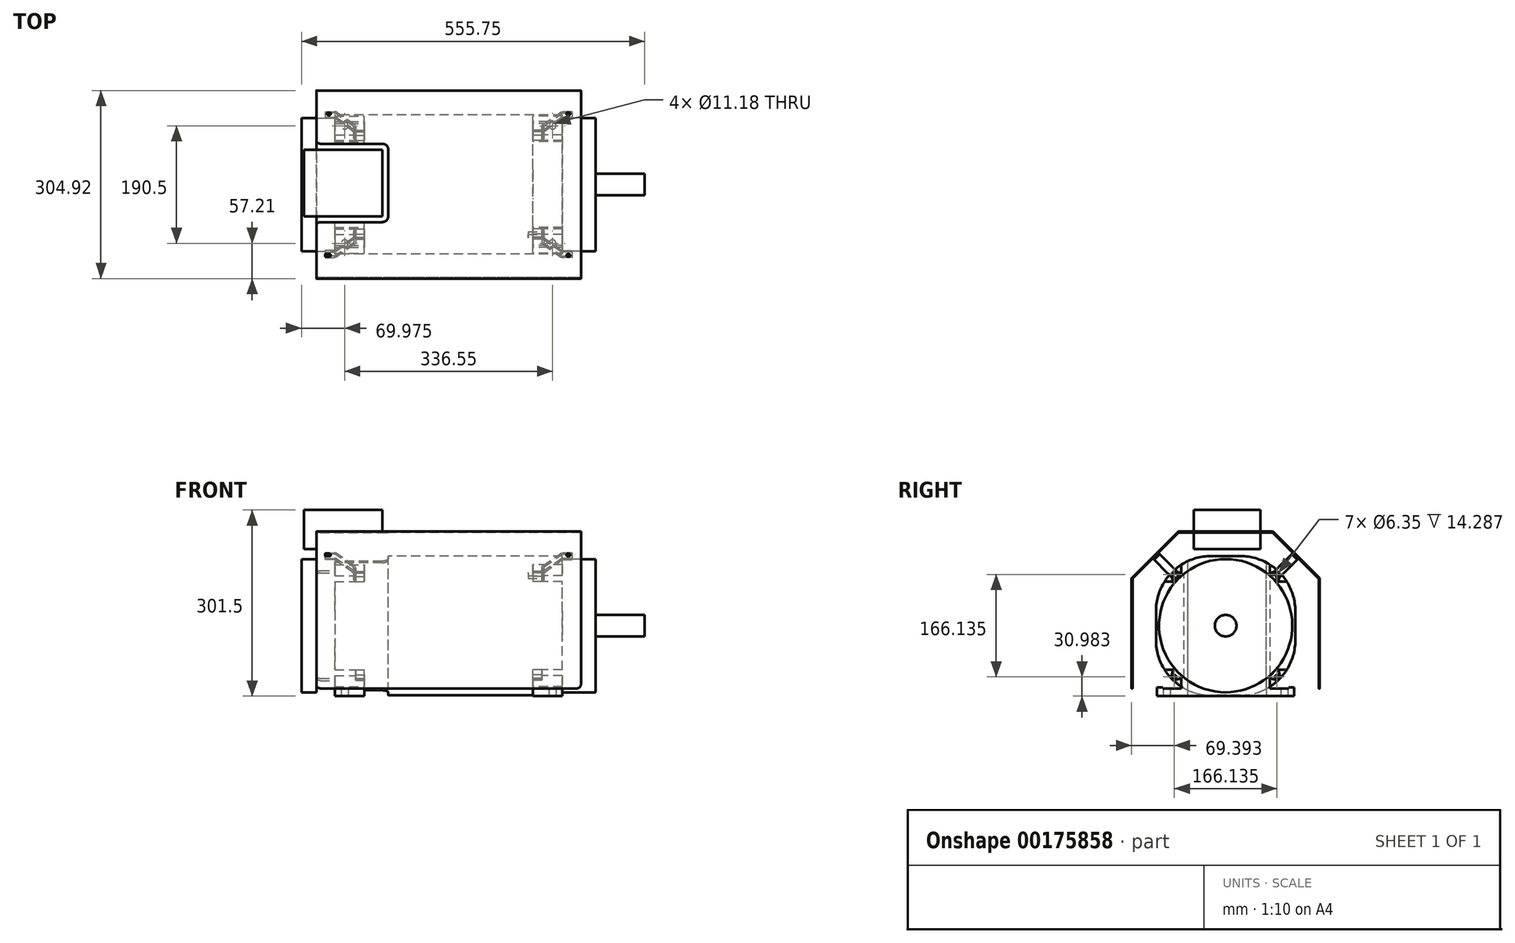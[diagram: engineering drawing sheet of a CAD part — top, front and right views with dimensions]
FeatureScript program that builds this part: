
annotation { "Feature Type Name" : "Feature", "Feature Type Description" : "" }
export const myFeature = defineFeature(function(context is Context, id is Id, definition is map)
    precondition{}
    {
        {
            var Q0;
            Q0=qCreatedBy(makeId("Right.planeOp"),FACE);
            var sketch = newSketch(context, id + "F0", { "sketchPlane" : qUnion([Q0])});
            skLineSegment(sketch, "E0.bottom", {"start": v(23.88, 112.78) * mm, "end": v(-23.88, 112.78) * mm});
            skLineSegment(sketch, "E0.top", {"start": v(23.88, -112.78) * mm, "end": v(-23.88, -112.78) * mm});
            skLineSegment(sketch, "E0.left", {"start": v(112.78, 23.88) * mm, "end": v(112.78, -23.88) * mm});
            skLineSegment(sketch, "E0.right", {"start": v(-112.78, 23.88) * mm, "end": v(-112.78, -23.88) * mm});
            skPoint(sketch, "E0.middle", {"position": v(0, 0) * mm});
            skPoint(sketch, "E1.visualSharp", {"position": v(112.78, 112.78) * mm});
            skArc(sketch, "E1.filletArc", {"start": v(112.78, 23.88) * mm, "mid": v(86.74, 86.74) * mm, "end": v(23.88, 112.78) * mm});
            skPoint(sketch, "E2.visualSharp", {"position": v(112.78, -112.78) * mm});
            skArc(sketch, "E2.filletArc", {"start": v(23.88, -112.78) * mm, "mid": v(86.74, -86.74) * mm, "end": v(112.78, -23.88) * mm});
            skPoint(sketch, "E3.visualSharp", {"position": v(-112.78, -112.78) * mm});
            skArc(sketch, "E3.filletArc", {"start": v(-112.78, -23.88) * mm, "mid": v(-86.74, -86.74) * mm, "end": v(-23.88, -112.78) * mm});
            skPoint(sketch, "E4.visualSharp", {"position": v(-112.78, 112.78) * mm});
            skArc(sketch, "E4.filletArc", {"start": v(-23.88, 112.78) * mm, "mid": v(-86.74, 86.74) * mm, "end": v(-112.78, 23.88) * mm});
            skSolve(sketch);
        }
        {
            var Q0;
            Q0 = qSketchRegion(id + "F0", true);
            extrude(context, id + "F1", {"entities" : qUnion([Q0]), "endBound" : BoundingType.SYMMETRIC, "depth" : 273.05 * mm});
        }
        {
            var Q0;
            Q0=makeQuery(id+"F1.opExtrude","CAP_FACE",FACE,{"disambiguationData":[OSD([sQuery(id+"F0.wireOp",EDGE,"E0.bottom"),sQuery(id+"F0.wireOp",EDGE,"E0.top"),sQuery(id+"F0.wireOp",EDGE,"E0.left"),sQuery(id+"F0.wireOp",EDGE,"E0.right"),sQuery(id+"F0.wireOp",EDGE,"E1.filletArc"),sQuery(id+"F0.wireOp",EDGE,"E2.filletArc"),sQuery(id+"F0.wireOp",EDGE,"E3.filletArc"),sQuery(id+"F0.wireOp",EDGE,"E4.filletArc")])],"isStart":false});
            var sketch = newSketch(context, id + "F2", { "sketchPlane" : qUnion([Q0])});
            skLineSegment(sketch, "E5.0", {"start": v(23.88, 112.78) * mm, "end": v(-23.88, 112.78) * mm});
            skArc(sketch, "E6.0", {"start": v(-23.88, 112.78) * mm, "mid": v(-86.74, 86.74) * mm, "end": v(-112.78, 23.88) * mm});
            skLineSegment(sketch, "E6.1", {"start": v(-112.78, 23.88) * mm, "end": v(-112.78, -23.88) * mm});
            skArc(sketch, "E6.2", {"start": v(-112.78, -23.88) * mm, "mid": v(-86.74, -86.74) * mm, "end": v(-23.88, -112.78) * mm});
            skLineSegment(sketch, "E6.3", {"start": v(23.88, -112.78) * mm, "end": v(-23.88, -112.78) * mm});
            skArc(sketch, "E6.4", {"start": v(23.88, -112.78) * mm, "mid": v(86.74, -86.74) * mm, "end": v(112.78, -23.88) * mm});
            skLineSegment(sketch, "E6.5", {"start": v(112.78, 23.88) * mm, "end": v(112.78, -23.88) * mm});
            skArc(sketch, "E6.6", {"start": v(112.78, 23.88) * mm, "mid": v(86.74, 86.74) * mm, "end": v(23.88, 112.78) * mm});
            skLineSegment(sketch, "E7.bottom", {"start": v(-101.82, 71.66) * mm, "end": v(-71.66, 71.66) * mm});
            skLineSegment(sketch, "E7.top", {"start": v(-101.82, 101.82) * mm, "end": v(-71.66, 101.82) * mm});
            skLineSegment(sketch, "E7.left", {"start": v(-101.82, 71.66) * mm, "end": v(-101.82, 101.82) * mm});
            skLineSegment(sketch, "E7.right", {"start": v(-71.66, 71.66) * mm, "end": v(-71.66, 101.82) * mm});
            skPoint(sketch, "E7.middle", {"position": v(-86.74, 86.74) * mm});
            skCircle(sketch, "E8", {"center": v(0, 0) * mm, "radius": 107.95 * mm});
            skLineSegment(sketch, "E9.1.0", {"start": v(-101.82, -101.82) * mm, "end": v(-101.82, -71.66) * mm});
            skLineSegment(sketch, "E9.1.1", {"start": v(-71.66, -101.82) * mm, "end": v(-101.82, -101.82) * mm});
            skLineSegment(sketch, "E9.1.2", {"start": v(-71.66, -101.82) * mm, "end": v(-71.66, -71.66) * mm});
            skLineSegment(sketch, "E9.1.3", {"start": v(-71.66, -71.66) * mm, "end": v(-101.82, -71.66) * mm});
            skLineSegment(sketch, "E9.2.0", {"start": v(101.82, -101.82) * mm, "end": v(71.66, -101.82) * mm});
            skLineSegment(sketch, "E9.2.1", {"start": v(101.82, -71.66) * mm, "end": v(101.82, -101.82) * mm});
            skLineSegment(sketch, "E9.2.2", {"start": v(101.82, -71.66) * mm, "end": v(71.66, -71.66) * mm});
            skLineSegment(sketch, "E9.2.3", {"start": v(71.66, -71.66) * mm, "end": v(71.66, -101.82) * mm});
            skLineSegment(sketch, "E9.3.0", {"start": v(101.82, 101.82) * mm, "end": v(101.82, 71.66) * mm});
            skLineSegment(sketch, "E9.3.1", {"start": v(71.66, 101.82) * mm, "end": v(101.82, 101.82) * mm});
            skLineSegment(sketch, "E9.3.2", {"start": v(71.66, 101.82) * mm, "end": v(71.66, 71.66) * mm});
            skLineSegment(sketch, "E9.3.3", {"start": v(71.66, 71.66) * mm, "end": v(101.82, 71.66) * mm});
            skLineSegment(sketch, "E10.bottom", {"start": v(-111, -114.05) * mm, "end": v(111, -114.05) * mm});
            skLineSegment(sketch, "E10.top", {"start": v(-111, -100.08) * mm, "end": v(111, -100.08) * mm});
            skLineSegment(sketch, "E10.left", {"start": v(-111, -114.05) * mm, "end": v(-111, -100.08) * mm});
            skLineSegment(sketch, "E10.right", {"start": v(111, -114.05) * mm, "end": v(111, -100.08) * mm});
            skLineSegment(sketch, "E11", {"start": v(0, -114.05) * mm, "end": v(0, -112.78) * mm});
            skPoint(sketch, "E11.endSnap0", {"position": v(0, -100.08) * mm});
            skSolve(sketch);
        }
        {
            var Q0;
            {var subQ9=sQuery(id+"F2.wireOp",EDGE,"E6.1");Q0=makeQuery(id+"F2.imprint","IMPRINT",FACE,{"disambiguationData":[TD([[makeQuery(id+"F2.imprint","IMPRINT",EDGE,{"derivedFrom":subQ9}),1.0]])]});}
            var Q1;
            {var subQ15=sQuery(id+"F2.wireOp",EDGE,"E7.right");var subQ16=sQuery(id+"F2.wireOp",EDGE,"E7.bottom");var subQ17=makeQuery(id+"F2.imprint","INTERSECT",VERTEX,{"derivedFrom":[subQ16,subQ15]});Q1=makeQuery(id+"F2.imprint","IMPRINT",FACE,{"disambiguationData":[TD([[makeQuery(id+"F2.imprint","IMPRINT",EDGE,{"disambiguationData":[TD([[subQ17,1.0]])],"derivedFrom":subQ16}),-1.0]])]});}
            var Q2;
            {var subQ6=sQuery(id+"F2.wireOp",EDGE,"E6.5");Q2=makeQuery(id+"F2.imprint","IMPRINT",FACE,{"disambiguationData":[TD([[makeQuery(id+"F2.imprint","IMPRINT",EDGE,{"derivedFrom":subQ6}),-1.0]])]});}
            var Q3;
            {var subQ8=sQuery(id+"F2.wireOp",EDGE,"E5.0");Q3=makeQuery(id+"F2.imprint","IMPRINT",FACE,{"disambiguationData":[TD([[makeQuery(id+"F2.imprint","IMPRINT",EDGE,{"derivedFrom":subQ8}),1.0]])]});}
            var Q4;
            {var subQ5=sQuery(id+"F2.wireOp",EDGE,"E6.3");Q4=makeQuery(id+"F2.imprint","IMPRINT",FACE,{"disambiguationData":[TD([[makeQuery(id+"F2.imprint","IMPRINT",EDGE,{"derivedFrom":subQ5}),-1.0]])]});}
            var Q5;
            {var subQ0=sQuery(id+"F2.wireOp",EDGE,"E9.1.3");var subQ1=sQuery(id+"F2.wireOp",EDGE,"E8");var subQ2=makeQuery(id+"F2.imprint","INTERSECT",VERTEX,{"derivedFrom":[subQ1,subQ0]});Q5=makeQuery(id+"F2.imprint","IMPRINT",FACE,{"disambiguationData":[TD([[makeQuery(id+"F2.imprint","IMPRINT",EDGE,{"disambiguationData":[TD([[subQ2,-1.0]])],"derivedFrom":subQ1}),1.0]])]});}
            var Q6;
            {var subQ0=sQuery(id+"F2.wireOp",EDGE,"E7.right");var subQ1=sQuery(id+"F2.wireOp",EDGE,"E7.bottom");var subQ2=makeQuery(id+"F2.imprint","INTERSECT",VERTEX,{"derivedFrom":[subQ1,subQ0]});Q6=makeQuery(id+"F2.imprint","IMPRINT",FACE,{"disambiguationData":[TD([[makeQuery(id+"F2.imprint","IMPRINT",EDGE,{"disambiguationData":[TD([[subQ2,1.0]])],"derivedFrom":subQ1}),1.0]])]});}
            var Q7;
            {var subQ0=sQuery(id+"F2.wireOp",EDGE,"E9.3.2");var subQ1=sQuery(id+"F2.wireOp",EDGE,"E8");var subQ2=makeQuery(id+"F2.imprint","INTERSECT",VERTEX,{"derivedFrom":[subQ1,subQ0]});Q7=makeQuery(id+"F2.imprint","IMPRINT",FACE,{"disambiguationData":[TD([[makeQuery(id+"F2.imprint","IMPRINT",EDGE,{"disambiguationData":[TD([[subQ2,1.0]])],"derivedFrom":subQ1}),1.0]])]});}
            var Q8;
            {var subQ0=sQuery(id+"F2.wireOp",EDGE,"E9.2.3");var subQ1=sQuery(id+"F2.wireOp",EDGE,"E8");var subQ2=makeQuery(id+"F2.imprint","INTERSECT",VERTEX,{"derivedFrom":[subQ1,subQ0]});Q8=makeQuery(id+"F2.imprint","IMPRINT",FACE,{"disambiguationData":[TD([[makeQuery(id+"F2.imprint","IMPRINT",EDGE,{"disambiguationData":[TD([[subQ2,-1.0]])],"derivedFrom":subQ1}),1.0]])]});}
            var Q9;
            {var subQ0=sQuery(id+"F2.wireOp",EDGE,"E9.1.2");var subQ1=sQuery(id+"F2.wireOp",EDGE,"E6.2");var subQ2=makeQuery(id+"F2.imprint","INTERSECT",VERTEX,{"derivedFrom":[subQ1,subQ0]});Q9=makeQuery(id+"F2.imprint","IMPRINT",FACE,{"disambiguationData":[TD([[makeQuery(id+"F2.imprint","IMPRINT",EDGE,{"disambiguationData":[TD([[subQ2,-1.0]])],"derivedFrom":subQ1}),1.0]])]});}
            var Q10;
            {var subQ0=sQuery(id+"F2.wireOp",EDGE,"E10.top");var subQ1=sQuery(id+"F2.wireOp",EDGE,"E6.4");var subQ2=makeQuery(id+"F2.imprint","INTERSECT",VERTEX,{"derivedFrom":[subQ1,subQ0]});Q10=makeQuery(id+"F2.imprint","IMPRINT",FACE,{"disambiguationData":[TD([[makeQuery(id+"F2.imprint","IMPRINT",EDGE,{"disambiguationData":[TD([[subQ2,-1.0]])],"derivedFrom":subQ1}),1.0]])]});}
            var Q11;
            {var subQ0=sQuery(id+"F2.wireOp",EDGE,"E10.right");Q11=makeQuery(id+"F2.imprint","IMPRINT",FACE,{"disambiguationData":[TD([[makeQuery(id+"F2.imprint","IMPRINT",EDGE,{"derivedFrom":subQ0}),1.0]])]});}
            var Q12;
            {var subQ0=sQuery(id+"F2.wireOp",EDGE,"E10.left");Q12=makeQuery(id+"F2.imprint","IMPRINT",FACE,{"disambiguationData":[TD([[makeQuery(id+"F2.imprint","IMPRINT",EDGE,{"derivedFrom":subQ0}),-1.0]])]});}
            var Q13;
            {var subQ0=sQuery(id+"F2.wireOp",EDGE,"E10.top");var subQ1=sQuery(id+"F2.wireOp",EDGE,"E8");var subQ2=makeQuery(id+"F2.imprint","INTERSECT",VERTEX,{"disambiguationData":[OD(0.0)],"derivedFrom":[subQ1,subQ0]});Q13=makeQuery(id+"F2.imprint","IMPRINT",FACE,{"disambiguationData":[TD([[makeQuery(id+"F2.imprint","IMPRINT",EDGE,{"disambiguationData":[TD([[subQ2,-1.0]])],"derivedFrom":subQ1}),1.0]])]});}
            extrude(context, id + "F3", {"entities" : qUnion([Q0, Q1, Q2, Q3, Q4, Q5, Q6, Q7, Q8, Q9, Q10, Q11, Q12, Q13]), "depth" : 47.75 * mm});
        }
        {
            var Q0;
            Q0=makeQuery(id+"F3.opExtrude","SWEPT_BODY",BODY,{"disambiguationData":[OSD([sQuery(id+"F2.wireOp",EDGE,"E5.0"),sQuery(id+"F2.wireOp",EDGE,"E6.0"),sQuery(id+"F2.wireOp",EDGE,"E6.1"),sQuery(id+"F2.wireOp",EDGE,"E6.2"),sQuery(id+"F2.wireOp",EDGE,"E6.3"),sQuery(id+"F2.wireOp",EDGE,"E6.4"),sQuery(id+"F2.wireOp",EDGE,"E6.5"),sQuery(id+"F2.wireOp",EDGE,"E6.6"),sQuery(id+"F2.wireOp",EDGE,"E7.bottom"),sQuery(id+"F2.wireOp",EDGE,"E7.right"),sQuery(id+"F2.wireOp",EDGE,"E8"),sQuery(id+"F2.wireOp",EDGE,"E9.1.2"),sQuery(id+"F2.wireOp",EDGE,"E9.1.3"),sQuery(id+"F2.wireOp",EDGE,"E9.2.2"),sQuery(id+"F2.wireOp",EDGE,"E9.2.3"),sQuery(id+"F2.wireOp",EDGE,"E9.3.2"),sQuery(id+"F2.wireOp",EDGE,"E9.3.3")])]});
            var Q1;
            Q1=qCreatedBy(makeId("Right.planeOp"),FACE);
            mirror(context, id + "F4", {"operationType" : NewBodyOperationType.ADD, "entities" : qUnion([Q0]), "mirrorPlane" : qUnion([Q1])});
        }
        {
            var Q0;
            Q0=makeQuery(id+"F3.opExtrude","SWEPT_FACE",FACE,{"disambiguationData":[OSD([sQuery(id+"F2.wireOp",EDGE,"E10.bottom")])]});
            var sketch = newSketch(context, id + "F5", { "sketchPlane" : qUnion([Q0])});
            skLineSegment(sketch, "E12", {"start": v(0, 0) * mm, "end": v(168.28, 0) * mm, "construction": true});
            skPoint(sketch, "E12.endSnap0", {"position": v(136.53, 0) * mm});
            skLineSegment(sketch, "E13", {"start": v(168.28, 0) * mm, "end": v(168.28, -95.25) * mm, "construction": true});
            skCircle(sketch, "E14", {"center": v(168.28, -95.25) * mm, "radius": 5.59 * mm});
            skCircle(sketch, "E15.MirrorC", {"center": v(168.28, 95.25) * mm, "radius": 5.59 * mm});
            skLineSegment(sketch, "E16", {"start": v(0, 0) * mm, "end": v(0, -142.84) * mm, "construction": true});
            skCircle(sketch, "E17.MirrorC", {"center": v(-168.28, 95.25) * mm, "radius": 5.59 * mm});
            skCircle(sketch, "E18.MirrorC", {"center": v(-168.28, -95.25) * mm, "radius": 5.59 * mm});
            skSolve(sketch);
        }
        {
            var Q0;
            Q0 = qSketchRegion(id + "F5", true);
            extrude(context, id + "F6", {"entities" : qUnion([Q0]), "operationType" : NewBodyOperationType.REMOVE, "oppositeDirection" : true, "depth" : 25.4 * mm});
        }
        {
            var Q0;
            Q0=makeQuery(id+"F3.opExtrude","CAP_FACE",FACE,{"disambiguationData":[OSD([sQuery(id+"F2.wireOp",EDGE,"E5.0"),sQuery(id+"F2.wireOp",EDGE,"E6.0"),sQuery(id+"F2.wireOp",EDGE,"E6.1"),sQuery(id+"F2.wireOp",EDGE,"E6.2"),sQuery(id+"F2.wireOp",EDGE,"E6.4"),sQuery(id+"F2.wireOp",EDGE,"E6.5"),sQuery(id+"F2.wireOp",EDGE,"E6.6"),sQuery(id+"F2.wireOp",EDGE,"E7.bottom"),sQuery(id+"F2.wireOp",EDGE,"E7.right"),sQuery(id+"F2.wireOp",EDGE,"E8"),sQuery(id+"F2.wireOp",EDGE,"E9.1.2"),sQuery(id+"F2.wireOp",EDGE,"E9.1.3"),sQuery(id+"F2.wireOp",EDGE,"E9.2.2"),sQuery(id+"F2.wireOp",EDGE,"E9.2.3"),sQuery(id+"F2.wireOp",EDGE,"E9.3.2"),sQuery(id+"F2.wireOp",EDGE,"E9.3.3"),sQuery(id+"F2.wireOp",EDGE,"E10.bottom"),sQuery(id+"F2.wireOp",EDGE,"E10.top"),sQuery(id+"F2.wireOp",EDGE,"E10.left"),sQuery(id+"F2.wireOp",EDGE,"E10.right")])],"isStart":false});
            var sketch = newSketch(context, id + "F7", { "sketchPlane" : qUnion([Q0])});
            skCircle(sketch, "E19", {"center": v(0, 0) * mm, "radius": 107.95 * mm});
            skSolve(sketch);
        }
        {
            var Q0;
            Q0 = qSketchRegion(id + "F7", true);
            extrude(context, id + "F8", {"entities" : qUnion([Q0]), "depth" : 53.97 * mm});
        }
        {
            var Q0;
            Q0=makeQuery(id+"F8.opExtrude","SWEPT_BODY",BODY,{"disambiguationData":[OSD([sQuery(id+"F7.wireOp",EDGE,"E19")])]});
            var Q1;
            Q1=qCreatedBy(makeId("Right.planeOp"),FACE);
            mirror(context, id + "F9", {"operationType" : NewBodyOperationType.ADD, "entities" : qUnion([Q0]), "mirrorPlane" : qUnion([Q1])});
        }
        {
            var Q0;
            Q0=makeQuery(id+"F8.opExtrude","CAP_FACE",FACE,{"disambiguationData":[OSD([sQuery(id+"F7.wireOp",EDGE,"E19")])],"isStart":false});
            var sketch = newSketch(context, id + "F10", { "sketchPlane" : qUnion([Q0])});
            skCircle(sketch, "E20", {"center": v(0, 0) * mm, "radius": 17.46 * mm});
            skSolve(sketch);
        }
        {
            var Q0;
            Q0 = qSketchRegion(id + "F10", true);
            extrude(context, id + "F11", {"entities" : qUnion([Q0]), "operationType" : NewBodyOperationType.ADD, "depth" : 79.25 * mm});
        }
        {
            var Q0;
            {var subQ5=sQuery(id+"F0.wireOp",EDGE,"E4.filletArc");Q0=makeQuery(id+"F4.boolean.opBoolean","SPLIT",FACE,{"disambiguationData":[TD([makeQuery(id+"F1.opExtrude","SWEPT_FACE",FACE,{"disambiguationData":[OSD([subQ5])]})])],"derivedFrom":makeQuery(id+"F1.opExtrude","CAP_FACE",FACE,{"disambiguationData":[OSD([sQuery(id+"F0.wireOp",EDGE,"E0.bottom"),sQuery(id+"F0.wireOp",EDGE,"E0.top"),sQuery(id+"F0.wireOp",EDGE,"E0.left"),sQuery(id+"F0.wireOp",EDGE,"E0.right"),sQuery(id+"F0.wireOp",EDGE,"E1.filletArc"),sQuery(id+"F0.wireOp",EDGE,"E2.filletArc"),sQuery(id+"F0.wireOp",EDGE,"E3.filletArc"),subQ5])],"isStart":false})});}
            var sketch = newSketch(context, id + "F12", { "sketchPlane" : qUnion([Q0])});
            skCircle(sketch, "E21", {"center": v(0, 0) * mm, "radius": 117.48 * mm, "construction": true});
            skCircle(sketch, "E22", {"center": v(-83.07, 83.07) * mm, "radius": 3.18 * mm});
            skLineSegment(sketch, "E23", {"start": v(0, 0) * mm, "end": v(-81.07, 0) * mm, "construction": true});
            skLineSegment(sketch, "E24", {"start": v(0, 0) * mm, "end": v(-83.07, 83.07) * mm, "construction": true});
            skArc(sketch, "E25", {"start": v(-81.72, 88.08) * mm, "mid": v(-86.74, 86.74) * mm, "end": v(-88.08, 81.72) * mm});
            skLineSegment(sketch, "E26", {"start": v(-88.08, 81.72) * mm, "end": v(-85.38, 71.66) * mm});
            skLineSegment(sketch, "E27.MirrorCS", {"start": v(-81.72, 88.08) * mm, "end": v(-71.66, 85.38) * mm});
            skArc(sketch, "E28.0", {"start": v(-71.66, 80.74) * mm, "mid": v(-76.33, 76.33) * mm, "end": v(-80.74, 71.66) * mm});
            skLineSegment(sketch, "E29.0", {"start": v(-71.66, 80.74) * mm, "end": v(-71.66, 93.09) * mm});
            skLineSegment(sketch, "E30.trimOffspring", {"start": v(-85.38, 71.66) * mm, "end": v(-80.74, 71.66) * mm});
            skPoint(sketch, "E31.0.start.orphan", {"position": v(-98.84, 71.66) * mm});
            skPoint(sketch, "E32.orphan", {"position": v(-71.66, 98.84) * mm});
            skSolve(sketch);
        }
        {
            var Q0;
            Q0 = qSketchRegion(id + "F12", true);
            extrude(context, id + "F13", {"entities" : qUnion([Q0]), "depth" : 14.29 * mm});
        }
        {
            var Q0;
            Q0=qCreatedBy(makeId("Front.planeOp"),FACE);
            var sketch = newSketch(context, id + "F14", { "sketchPlane" : qUnion([Q0])});
            skLineSegment(sketch, "E33", {"start": v(0, 0) * mm, "end": v(268.97, 0) * mm, "construction": true});
            skSolve(sketch);
        }
        {
            var Q0;
            Q0=makeQuery(id+"F13.opExtrude","SWEPT_BODY",BODY,{"disambiguationData":[OSD([sQuery(id+"F12.wireOp",EDGE,"E22"),sQuery(id+"F12.wireOp",EDGE,"E25"),sQuery(id+"F12.wireOp",EDGE,"E26"),sQuery(id+"F12.wireOp",EDGE,"E27.MirrorCS"),sQuery(id+"F12.wireOp",EDGE,"E28.0"),sQuery(id+"F12.wireOp",EDGE,"E29.0"),sQuery(id+"F12.wireOp",EDGE,"E30.trimOffspring")])]});
            var Q1;
            Q1=sQuery(id+"F14.wireOp",EDGE,"E33");
            circularPattern(context, id + "F15", {"entities" : qUnion([Q0]), "axis" : qUnion([Q1]), "angle" : 360 * degree, "instanceCount" : 4, "equalSpace" : true});
        }
        {
            var Q0;
            Q0=makeQuery(id+"F13.opExtrude","SWEPT_BODY",BODY,{"disambiguationData":[OSD([sQuery(id+"F12.wireOp",EDGE,"E22"),sQuery(id+"F12.wireOp",EDGE,"E25"),sQuery(id+"F12.wireOp",EDGE,"E26"),sQuery(id+"F12.wireOp",EDGE,"E27.MirrorCS"),sQuery(id+"F12.wireOp",EDGE,"E28.0"),sQuery(id+"F12.wireOp",EDGE,"E29.0"),sQuery(id+"F12.wireOp",EDGE,"E30.trimOffspring")])]});
            var Q1;
            Q1=makeQuery(id+"F15.opPattern","COPY",BODY,{"derivedFrom":makeQuery(id+"F13.opExtrude","SWEPT_BODY",BODY,{"disambiguationData":[OSD([sQuery(id+"F12.wireOp",EDGE,"E22"),sQuery(id+"F12.wireOp",EDGE,"E25"),sQuery(id+"F12.wireOp",EDGE,"E26"),sQuery(id+"F12.wireOp",EDGE,"E27.MirrorCS"),sQuery(id+"F12.wireOp",EDGE,"E28.0"),sQuery(id+"F12.wireOp",EDGE,"E29.0"),sQuery(id+"F12.wireOp",EDGE,"E30.trimOffspring")])]}),"instanceName":"1"});
            var Q2;
            Q2=makeQuery(id+"F15.opPattern","COPY",BODY,{"derivedFrom":makeQuery(id+"F13.opExtrude","SWEPT_BODY",BODY,{"disambiguationData":[OSD([sQuery(id+"F12.wireOp",EDGE,"E22"),sQuery(id+"F12.wireOp",EDGE,"E25"),sQuery(id+"F12.wireOp",EDGE,"E26"),sQuery(id+"F12.wireOp",EDGE,"E27.MirrorCS"),sQuery(id+"F12.wireOp",EDGE,"E28.0"),sQuery(id+"F12.wireOp",EDGE,"E29.0"),sQuery(id+"F12.wireOp",EDGE,"E30.trimOffspring")])]}),"instanceName":"3"});
            var Q3;
            Q3=makeQuery(id+"F15.opPattern","COPY",BODY,{"derivedFrom":makeQuery(id+"F13.opExtrude","SWEPT_BODY",BODY,{"disambiguationData":[OSD([sQuery(id+"F12.wireOp",EDGE,"E22"),sQuery(id+"F12.wireOp",EDGE,"E25"),sQuery(id+"F12.wireOp",EDGE,"E26"),sQuery(id+"F12.wireOp",EDGE,"E27.MirrorCS"),sQuery(id+"F12.wireOp",EDGE,"E28.0"),sQuery(id+"F12.wireOp",EDGE,"E29.0"),sQuery(id+"F12.wireOp",EDGE,"E30.trimOffspring")])]}),"instanceName":"2"});
            var Q4;
            Q4=qCreatedBy(makeId("Right.planeOp"),FACE);
            mirror(context, id + "F16", {"operationType" : NewBodyOperationType.ADD, "entities" : qUnion([Q0, Q1, Q2, Q3]), "mirrorPlane" : qUnion([Q4])});
        }
        {
            var Q0;
            Q0=qCreatedBy(makeId("Right.planeOp"),FACE);
            cPlane(context, id + "F17", {"entities" : qUnion([Q0]), "cplaneType" : CPlaneType.OFFSET, "offset" : 170.8 * mm, "oppositeDirection" : true, "width" : 152.4 * mm, "height" : 152.4 * mm});
        }
        {
            var Q0;
            Q0=qCreatedBy(id+"F17.planeOp",FACE);
            var sketch = newSketch(context, id + "F18", { "sketchPlane" : qUnion([Q0])});
            skLineSegment(sketch, "E34.0", {"start": v(23.88, 112.78) * mm, "end": v(-23.88, 112.78) * mm, "construction": true});
            skLineSegment(sketch, "E35", {"start": v(0, 112.78) * mm, "end": v(0, 187.45) * mm, "construction": true});
            skPoint(sketch, "E35.endSnap0", {"position": v(0, 112.78) * mm});
            skLineSegment(sketch, "E36", {"start": v(0, 187.45) * mm, "end": v(-51.3, 187.45) * mm, "construction": true});
            skLineSegment(sketch, "E37", {"start": v(-51.3, 187.45) * mm, "end": v(56.64, 187.45) * mm});
            skLineSegment(sketch, "E38", {"start": v(56.64, 187.45) * mm, "end": v(56.64, 123.95) * mm});
            skLineSegment(sketch, "E39", {"start": v(56.64, 123.95) * mm, "end": v(-51.3, 123.95) * mm});
            skLineSegment(sketch, "E40", {"start": v(-51.3, 123.95) * mm, "end": v(-51.3, 187.45) * mm});
            skLineSegment(sketch, "E41", {"start": v(23.88, 123.95) * mm, "end": v(23.88, 98.55) * mm});
            skLineSegment(sketch, "E42", {"start": v(23.88, 98.55) * mm, "end": v(-23.88, 98.55) * mm});
            skLineSegment(sketch, "E43", {"start": v(-23.88, 98.55) * mm, "end": v(-23.88, 123.95) * mm});
            skSolve(sketch);
        }
        {
            var Q0;
            Q0=makeQuery(id+"F18.imprint","IMPRINT",FACE,{"disambiguationData":[TD([[makeQuery(id+"F18.imprint","IMPRINT",EDGE,{"derivedFrom":sQuery(id+"F18.wireOp",EDGE,"E37")}),-1.0]])]});
            extrude(context, id + "F19", {"entities" : qUnion([Q0]), "endBound" : BoundingType.SYMMETRIC, "depth" : 127 * mm});
        }
        {
            var Q0;
            Q0 = qSketchRegion(id + "F18", true);
            extrude(context, id + "F20", {"entities" : qUnion([Q0]), "operationType" : NewBodyOperationType.ADD, "endBound" : BoundingType.SYMMETRIC, "depth" : 69.85 * mm});
        }
        {
            var Q0;
            Q0=makeQuery(id+"F15.opPattern","COPY",FACE,{"derivedFrom":makeQuery(id+"F13.opExtrude","CAP_FACE",FACE,{"disambiguationData":[OSD([sQuery(id+"F12.wireOp",EDGE,"E22"),sQuery(id+"F12.wireOp",EDGE,"E25"),sQuery(id+"F12.wireOp",EDGE,"E26"),sQuery(id+"F12.wireOp",EDGE,"E27.MirrorCS"),sQuery(id+"F12.wireOp",EDGE,"E28.0"),sQuery(id+"F12.wireOp",EDGE,"E29.0"),sQuery(id+"F12.wireOp",EDGE,"E30.trimOffspring")])],"isStart":false}),"instanceName":"3"});
            cPlane(context, id + "F21", {"entities" : qUnion([Q0]), "cplaneType" : CPlaneType.OFFSET, "offset" : 0 * mm, "width" : 152.4 * mm, "height" : 152.4 * mm});
        }
        {
            var Q0;
            Q0=qCreatedBy(id+"F21.planeOp",FACE);
            var sketch = newSketch(context, id + "F22", { "sketchPlane" : qUnion([Q0])});
            skLineSegment(sketch, "E44", {"start": v(-150.88, 150.88) * mm, "end": v(-76.32, 150.88) * mm, "construction": true});
            skLineSegment(sketch, "E45", {"start": v(0, 112.78) * mm, "end": v(0, 150.88) * mm, "construction": true});
            skPoint(sketch, "E45.endSnap0", {"position": v(0, 150.88) * mm});
            skLineSegment(sketch, "E46.0", {"start": v(23.88, 112.78) * mm, "end": v(-23.88, 112.78) * mm});
            skCircle(sketch, "E47.0", {"center": v(-83.07, 83.07) * mm, "radius": 3.18 * mm, "construction": true});
            skLineSegment(sketch, "E48.0", {"start": v(-112.78, 23.88) * mm, "end": v(-112.78, -23.88) * mm, "construction": true});
            skLineSegment(sketch, "E49", {"start": v(-112.78, 0) * mm, "end": v(-150.88, 0) * mm, "construction": true});
            skPoint(sketch, "E49.endSnap0", {"position": v(-112.78, 0) * mm});
            skLineSegment(sketch, "E50", {"start": v(-150.88, 150.88) * mm, "end": v(-150.88, 76.32) * mm, "construction": true});
            skLineSegment(sketch, "E51", {"start": v(-76.79, 150.41) * mm, "end": v(-150.41, 76.79) * mm});
            skLineSegment(sketch, "E52", {"start": v(-83.07, 83.07) * mm, "end": v(-113.6, 113.6) * mm, "construction": true});
            skLineSegment(sketch, "E53", {"start": v(-150.88, 75.67) * mm, "end": v(-150.88, -101.6) * mm});
            skLineSegment(sketch, "E54", {"start": v(-75.67, 150.88) * mm, "end": v(0, 150.88) * mm});
            skPoint(sketch, "E55.visualSharp", {"position": v(-76.32, 150.88) * mm});
            skArc(sketch, "E55.filletArc", {"start": v(-75.67, 150.88) * mm, "mid": v(-76.27, 150.76) * mm, "end": v(-76.79, 150.41) * mm});
            skPoint(sketch, "E56.visualSharp", {"position": v(-150.88, 76.32) * mm});
            skArc(sketch, "E56.filletArc", {"start": v(-150.41, 76.79) * mm, "mid": v(-150.76, 76.27) * mm, "end": v(-150.88, 75.67) * mm});
            skCircle(sketch, "E57.0", {"center": v(-83.07, -83.07) * mm, "radius": 3.18 * mm, "construction": true});
            skLineSegment(sketch, "E58.MirrorCS", {"start": v(150.88, 75.67) * mm, "end": v(150.88, -101.6) * mm});
            skArc(sketch, "E59.MirrorCS", {"start": v(150.41, 76.79) * mm, "mid": v(150.76, 76.27) * mm, "end": v(150.88, 75.67) * mm});
            skLineSegment(sketch, "E60.MirrorCS", {"start": v(75.67, 150.88) * mm, "end": v(0, 150.88) * mm});
            skLineSegment(sketch, "E61.MirrorCS", {"start": v(76.79, 150.41) * mm, "end": v(150.41, 76.79) * mm});
            skArc(sketch, "E62.MirrorCS", {"start": v(75.67, 150.88) * mm, "mid": v(76.27, 150.76) * mm, "end": v(76.79, 150.41) * mm});
            skLineSegment(sketch, "E63.0", {"start": v(-152.46, 75.67) * mm, "end": v(-152.46, -101.6) * mm});
            skArc(sketch, "E63.1", {"start": v(-151.53, 77.91) * mm, "mid": v(-152.22, 76.88) * mm, "end": v(-152.46, 75.67) * mm});
            skLineSegment(sketch, "E63.2", {"start": v(-77.91, 151.53) * mm, "end": v(-151.53, 77.91) * mm});
            skArc(sketch, "E63.3", {"start": v(-75.67, 152.46) * mm, "mid": v(-76.88, 152.22) * mm, "end": v(-77.91, 151.53) * mm});
            skLineSegment(sketch, "E63.4", {"start": v(-75.67, 152.46) * mm, "end": v(0, 152.46) * mm});
            skLineSegment(sketch, "E63.5", {"start": v(75.67, 152.46) * mm, "end": v(0, 152.46) * mm});
            skLineSegment(sketch, "E63.6", {"start": v(152.46, 75.67) * mm, "end": v(152.46, -101.6) * mm});
            skArc(sketch, "E63.7", {"start": v(151.53, 77.91) * mm, "mid": v(152.22, 76.88) * mm, "end": v(152.46, 75.67) * mm});
            skLineSegment(sketch, "E63.8", {"start": v(77.91, 151.53) * mm, "end": v(151.53, 77.91) * mm});
            skArc(sketch, "E63.9", {"start": v(75.67, 152.46) * mm, "mid": v(76.88, 152.22) * mm, "end": v(77.91, 151.53) * mm});
            skLineSegment(sketch, "E64", {"start": v(-150.88, -101.6) * mm, "end": v(-152.46, -101.6) * mm});
            skLineSegment(sketch, "E65", {"start": v(152.46, -101.6) * mm, "end": v(150.88, -101.6) * mm});
            skSolve(sketch);
        }
        {
            var Q0;
            Q0 = qSketchRegion(id + "F22", true);
            extrude(context, id + "F23", {"entities" : qUnion([Q0]), "depth" : 63.5 * mm, "hasSecondDirection" : true, "secondDirectionOppositeDirection" : true, "secondDirectionDepth" : 365.12 * mm});
        }
        {
            var Q0;
            Q0=makeQuery(id+"F23.opExtrude","SWEPT_FACE",FACE,{"disambiguationData":[OSD([sQuery(id+"F22.wireOp",EDGE,"E63.4"),sQuery(id+"F22.wireOp",EDGE,"E63.5")])]});
            var sketch = newSketch(context, id + "F24", { "sketchPlane" : qUnion([Q0])});
            skLineSegment(sketch, "E66.0.0", {"start": v(-107.31, 56.64) * mm, "end": v(-234.31, 56.64) * mm, "construction": true});
            skLineSegment(sketch, "E66.0.1", {"start": v(-234.31, 56.64) * mm, "end": v(-234.31, -51.3) * mm, "construction": true});
            skLineSegment(sketch, "E66.0.2", {"start": v(-234.31, -51.3) * mm, "end": v(-107.31, -51.3) * mm, "construction": true});
            skLineSegment(sketch, "E66.0.3", {"start": v(-107.31, -51.3) * mm, "end": v(-107.31, 56.64) * mm, "construction": true});
            skLineSegment(sketch, "E67", {"start": v(-234.31, 2.67) * mm, "end": v(-107.31, 2.67) * mm, "construction": true});
            skLineSegment(sketch, "E68.0", {"start": v(-107.31, 66.17) * mm, "end": v(-207.96, 66.17) * mm});
            skLineSegment(sketch, "E68.1", {"start": v(-97.79, -51.3) * mm, "end": v(-97.79, 56.64) * mm});
            skLineSegment(sketch, "E68.2", {"start": v(-207.96, -60.83) * mm, "end": v(-107.31, -60.83) * mm});
            skLineSegment(sketch, "E69", {"start": v(-214.31, -99.68) * mm, "end": v(-214.31, -67.18) * mm});
            skPoint(sketch, "E70.visualSharp", {"position": v(-97.79, -60.83) * mm});
            skArc(sketch, "E70.filletArc", {"start": v(-107.31, -60.83) * mm, "mid": v(-100.58, -58.04) * mm, "end": v(-97.79, -51.3) * mm});
            skPoint(sketch, "E71.visualSharp", {"position": v(-97.79, 66.17) * mm});
            skArc(sketch, "E71.filletArc", {"start": v(-97.79, 56.64) * mm, "mid": v(-100.58, 63.38) * mm, "end": v(-107.31, 66.17) * mm});
            skLineSegment(sketch, "E72", {"start": v(-214.31, -67.18) * mm, "end": v(-214.31, 72.52) * mm});
            skLineSegment(sketch, "E73", {"start": v(-214.31, 72.52) * mm, "end": v(-214.31, 100.57) * mm});
            skPoint(sketch, "E74.visualSharp", {"position": v(-214.31, -67.18) * mm});
            skArc(sketch, "E74.filletArc", {"start": v(-207.96, -60.83) * mm, "mid": v(-212.45, -62.7) * mm, "end": v(-214.31, -67.18) * mm});
            skPoint(sketch, "E75.visualSharp", {"position": v(-214.31, 72.52) * mm});
            skArc(sketch, "E75.filletArc", {"start": v(-214.31, 72.52) * mm, "mid": v(-212.45, 68.03) * mm, "end": v(-207.96, 66.17) * mm});
            skSolve(sketch);
        }
        {
            var Q0;
            {var subQ0=sQuery(id+"F24.wireOp",EDGE,"E68.0");Q0=makeQuery(id+"F24.imprint","IMPRINT",FACE,{"disambiguationData":[TD([[makeQuery(id+"F24.imprint","IMPRINT",EDGE,{"derivedFrom":subQ0}),1.0]])]});}
            extrude(context, id + "F25", {"entities" : qUnion([Q0]), "operationType" : NewBodyOperationType.REMOVE, "endBound" : BoundingType.THROUGH_ALL, "oppositeDirection" : true, "depth" : 25.4 * mm});
        }
        {
            var Q0;
            Q0=sQuery(id+"F14.wireOp",EDGE,"E33");
            cPlane(context, id + "F26", {"entities" : qUnion([Q0]), "cplaneType" : CPlaneType.LINE_ANGLE, "offset" : 25.4 * mm, "angle" : 45 * degree, "width" : 152.4 * mm, "height" : 152.4 * mm});
        }
        {
            var Q0;
            Q0=qCreatedBy(id+"F26.planeOp",FACE);
            var sketch = newSketch(context, id + "F27", { "sketchPlane" : qUnion([Q0])});
            skLineSegment(sketch, "E76.0", {"start": v(-150.81, 114.3) * mm, "end": v(-150.81, 120.65) * mm, "construction": true});
            skLineSegment(sketch, "E77.0", {"start": v(-214.31, 160.66) * mm, "end": v(214.31, 160.66) * mm});
            skLineSegment(sketch, "E78.0", {"start": v(-153.99, 111.12) * mm, "end": v(-153.99, 126.21) * mm});
            skLineSegment(sketch, "E79", {"start": v(-154.92, 128.46) * mm, "end": v(-183, 156.55) * mm});
            skLineSegment(sketch, "E80.0", {"start": v(-214.31, 157.48) * mm, "end": v(214.31, 157.48) * mm, "construction": true});
            skPoint(sketch, "E81.visualSharp", {"position": v(-153.99, 127.53) * mm});
            skArc(sketch, "E81.filletArc", {"start": v(-153.99, 126.21) * mm, "mid": v(-154.23, 127.43) * mm, "end": v(-154.92, 128.46) * mm});
            skPoint(sketch, "E82.0", {"position": v(-150.81, 122.67) * mm});
            skLineSegment(sketch, "E83", {"start": v(-185.25, 157.48) * mm, "end": v(-200.34, 157.48) * mm});
            skPoint(sketch, "E84.visualSharp", {"position": v(-183.94, 157.48) * mm});
            skArc(sketch, "E84.filletArc", {"start": v(-183, 156.55) * mm, "mid": v(-184.04, 157.24) * mm, "end": v(-185.25, 157.48) * mm});
            skLineSegment(sketch, "E85.0", {"start": v(-185.25, 160.66) * mm, "end": v(-200.34, 160.66) * mm});
            skLineSegment(sketch, "E85.1", {"start": v(-150.81, 111.12) * mm, "end": v(-150.81, 126.21) * mm});
            skArc(sketch, "E85.2", {"start": v(-150.81, 126.21) * mm, "mid": v(-151.3, 128.64) * mm, "end": v(-152.67, 130.7) * mm});
            skLineSegment(sketch, "E85.3", {"start": v(-152.67, 130.7) * mm, "end": v(-180.76, 158.8) * mm});
            skArc(sketch, "E85.4", {"start": v(-180.76, 158.8) * mm, "mid": v(-182.82, 160.17) * mm, "end": v(-185.25, 160.66) * mm});
            skLineSegment(sketch, "E86", {"start": v(-200.34, 160.66) * mm, "end": v(-200.34, 157.48) * mm});
            skLineSegment(sketch, "E87", {"start": v(-153.99, 111.12) * mm, "end": v(-150.81, 111.12) * mm});
            skSolve(sketch);
        }
        {
            var Q0;
            Q0 = qSketchRegion(id + "F27", true);
            extrude(context, id + "F28", {"entities" : qUnion([Q0]), "endBound" : BoundingType.SYMMETRIC, "depth" : 12.7 * mm});
        }
        {
            var Q0;
            Q0=makeQuery(id+"F28.opExtrude","SWEPT_FACE",FACE,{"disambiguationData":[OSD([sQuery(id+"F27.wireOp",EDGE,"E78.0")])]});
            var sketch = newSketch(context, id + "F29", { "sketchPlane" : qUnion([Q0])});
            skArc(sketch, "E88.0", {"start": v(-80.82, 85.31) * mm, "mid": v(-85.31, 85.31) * mm, "end": v(-85.31, 80.82) * mm});
            skLineSegment(sketch, "E89", {"start": v(-85.31, 80.82) * mm, "end": v(-80.82, 76.33) * mm});
            skLineSegment(sketch, "E90", {"start": v(-80.82, 85.31) * mm, "end": v(-76.33, 80.82) * mm});
            skLineSegment(sketch, "E91", {"start": v(-85.31, 80.82) * mm, "end": v(-80.82, 85.31) * mm, "construction": true});
            skLineSegment(sketch, "E92", {"start": v(-76.33, 80.82) * mm, "end": v(-80.82, 76.33) * mm});
            skSolve(sketch);
        }
        {
            var Q0;
            Q0 = qSketchRegion(id + "F29", true);
            extrude(context, id + "F30", {"entities" : qUnion([Q0]), "operationType" : NewBodyOperationType.REMOVE, "oppositeDirection" : true, "depth" : 25.4 * mm});
        }
        {
            var Q0;
            Q0=makeQuery(id+"F28.opExtrude","SWEPT_FACE",FACE,{"disambiguationData":[OSD([sQuery(id+"F27.wireOp",EDGE,"E83")])]});
            var sketch = newSketch(context, id + "F31", { "sketchPlane" : qUnion([Q0])});
            skArc(sketch, "E93", {"start": v(194, 3.18) * mm, "mid": v(190.82, 0) * mm, "end": v(194, -3.18) * mm});
            skPoint(sketch, "E93.centerSnap0", {"position": v(200.34, 0) * mm});
            skLineSegment(sketch, "E94", {"start": v(194, -3.18) * mm, "end": v(194, 3.18) * mm, "construction": true});
            skLineSegment(sketch, "E95", {"start": v(194, -3.17) * mm, "end": v(200.34, -3.17) * mm});
            skLineSegment(sketch, "E96", {"start": v(194, 3.18) * mm, "end": v(200.34, 3.18) * mm});
            skLineSegment(sketch, "E97", {"start": v(200.34, 3.17) * mm, "end": v(200.34, -3.17) * mm});
            skSolve(sketch);
        }
        {
            var Q0;
            Q0 = qSketchRegion(id + "F31", true);
            extrude(context, id + "F32", {"entities" : qUnion([Q0]), "operationType" : NewBodyOperationType.REMOVE, "oppositeDirection" : true, "depth" : 25.4 * mm});
        }
        {
            var Q0;
            Q0=makeQuery(id+"F28.opExtrude","SWEPT_BODY",BODY,{"disambiguationData":[OSD([sQuery(id+"F27.wireOp",EDGE,"E78.0"),sQuery(id+"F27.wireOp",EDGE,"E79"),sQuery(id+"F27.wireOp",EDGE,"E81.filletArc"),sQuery(id+"F27.wireOp",EDGE,"E83"),sQuery(id+"F27.wireOp",EDGE,"E84.filletArc"),sQuery(id+"F27.wireOp",EDGE,"E85.0"),sQuery(id+"F27.wireOp",EDGE,"E85.1"),sQuery(id+"F27.wireOp",EDGE,"E85.2"),sQuery(id+"F27.wireOp",EDGE,"E85.3"),sQuery(id+"F27.wireOp",EDGE,"E85.4"),sQuery(id+"F27.wireOp",EDGE,"E86"),sQuery(id+"F27.wireOp",EDGE,"E87")])]});
            var Q1;
            Q1=sQuery(id+"F14.wireOp",EDGE,"E33");
            circularPattern(context, id + "F33", {"entities" : qUnion([Q0]), "axis" : qUnion([Q1]), "angle" : 90 * degree, "instanceCount" : 2, "oppositeDirection" : true});
        }
        {
            var Q0;
            Q0=makeQuery(id+"F28.opExtrude","SWEPT_BODY",BODY,{"disambiguationData":[OSD([sQuery(id+"F27.wireOp",EDGE,"E78.0"),sQuery(id+"F27.wireOp",EDGE,"E79"),sQuery(id+"F27.wireOp",EDGE,"E81.filletArc"),sQuery(id+"F27.wireOp",EDGE,"E83"),sQuery(id+"F27.wireOp",EDGE,"E84.filletArc"),sQuery(id+"F27.wireOp",EDGE,"E85.0"),sQuery(id+"F27.wireOp",EDGE,"E85.1"),sQuery(id+"F27.wireOp",EDGE,"E85.2"),sQuery(id+"F27.wireOp",EDGE,"E85.3"),sQuery(id+"F27.wireOp",EDGE,"E85.4"),sQuery(id+"F27.wireOp",EDGE,"E86"),sQuery(id+"F27.wireOp",EDGE,"E87")])]});
            var Q1;
            Q1=makeQuery(id+"F33.opPattern","COPY",BODY,{"derivedFrom":makeQuery(id+"F28.opExtrude","SWEPT_BODY",BODY,{"disambiguationData":[OSD([sQuery(id+"F27.wireOp",EDGE,"E78.0"),sQuery(id+"F27.wireOp",EDGE,"E79"),sQuery(id+"F27.wireOp",EDGE,"E81.filletArc"),sQuery(id+"F27.wireOp",EDGE,"E83"),sQuery(id+"F27.wireOp",EDGE,"E84.filletArc"),sQuery(id+"F27.wireOp",EDGE,"E85.0"),sQuery(id+"F27.wireOp",EDGE,"E85.1"),sQuery(id+"F27.wireOp",EDGE,"E85.2"),sQuery(id+"F27.wireOp",EDGE,"E85.3"),sQuery(id+"F27.wireOp",EDGE,"E85.4"),sQuery(id+"F27.wireOp",EDGE,"E86"),sQuery(id+"F27.wireOp",EDGE,"E87")])]}),"instanceName":"1"});
            var Q2;
            Q2=qCreatedBy(makeId("Right.planeOp"),FACE);
            mirror(context, id + "F34", {"entities" : qUnion([Q0, Q1]), "mirrorPlane" : qUnion([Q2])});
        }
        {
            var Q0;
            Q0=makeQuery(id+"F23.opExtrude","SWEPT_FACE",FACE,{"disambiguationData":[OSD([sQuery(id+"F22.wireOp",EDGE,"E63.2")])]});
            var sketch = newSketch(context, id + "F35", { "sketchPlane" : qUnion([Q0])});
            skArc(sketch, "E98.0", {"start": v(194, -3.17) * mm, "mid": v(190.82, 0) * mm, "end": v(194, 3.18) * mm, "construction": true});
            skLineSegment(sketch, "E99", {"start": v(190.82, 0) * mm, "end": v(194, 0) * mm, "construction": true});
            skCircle(sketch, "E100", {"center": v(194, 0) * mm, "radius": 3.18 * mm});
            skSolve(sketch);
        }
        {
            var Q0;
            Q0 = qSketchRegion(id + "F35", true);
            extrude(context, id + "F36", {"entities" : qUnion([Q0]), "oppositeDirection" : true, "depth" : 25.4 * mm});
        }
        {
            var Q0;
            Q0=makeQuery(id+"F36.opExtrude","SWEPT_BODY",BODY,{"disambiguationData":[OSD([sQuery(id+"F35.wireOp",EDGE,"E100")])]});
            var Q1;
            Q1=qCreatedBy(makeId("Right.planeOp"),FACE);
            mirror(context, id + "F37", {"entities" : qUnion([Q0]), "mirrorPlane" : qUnion([Q1])});
        }
        {
            var Q0;
            Q0=makeQuery(id+"F36.opExtrude","SWEPT_BODY",BODY,{"disambiguationData":[OSD([sQuery(id+"F35.wireOp",EDGE,"E100")])]});
            var Q1;
            Q1=makeQuery(id+"F37.opPattern","COPY",BODY,{"derivedFrom":makeQuery(id+"F36.opExtrude","SWEPT_BODY",BODY,{"disambiguationData":[OSD([sQuery(id+"F35.wireOp",EDGE,"E100")])]}),"instanceName":"1"});
            var Q2;
            Q2=qCreatedBy(makeId("Front.planeOp"),FACE);
            mirror(context, id + "F38", {"entities" : qUnion([Q0, Q1]), "mirrorPlane" : qUnion([Q2])});
        }
        {
            var Q0;
            Q0=makeQuery(id+"F38.opPattern","COPY",BODY,{"derivedFrom":makeQuery(id+"F37.opPattern","COPY",BODY,{"derivedFrom":makeQuery(id+"F36.opExtrude","SWEPT_BODY",BODY,{"disambiguationData":[OSD([sQuery(id+"F35.wireOp",EDGE,"E100")])]}),"instanceName":"1"}),"instanceName":"1"});
            var Q1;
            Q1=makeQuery(id+"F38.opPattern","COPY",BODY,{"derivedFrom":makeQuery(id+"F36.opExtrude","SWEPT_BODY",BODY,{"disambiguationData":[OSD([sQuery(id+"F35.wireOp",EDGE,"E100")])]}),"instanceName":"1"});
            var Q2;
            Q2=makeQuery(id+"F37.opPattern","COPY",BODY,{"derivedFrom":makeQuery(id+"F36.opExtrude","SWEPT_BODY",BODY,{"disambiguationData":[OSD([sQuery(id+"F35.wireOp",EDGE,"E100")])]}),"instanceName":"1"});
            var Q3;
            Q3=makeQuery(id+"F36.opExtrude","SWEPT_BODY",BODY,{"disambiguationData":[OSD([sQuery(id+"F35.wireOp",EDGE,"E100")])]});
            var Q4;
            Q4=makeQuery(id+"F23.opExtrude","SWEPT_BODY",BODY,{"disambiguationData":[OSD([sQuery(id+"F22.wireOp",EDGE,"E51"),sQuery(id+"F22.wireOp",EDGE,"E53"),sQuery(id+"F22.wireOp",EDGE,"E54"),sQuery(id+"F22.wireOp",EDGE,"E55.filletArc"),sQuery(id+"F22.wireOp",EDGE,"E56.filletArc"),sQuery(id+"F22.wireOp",EDGE,"E58.MirrorCS"),sQuery(id+"F22.wireOp",EDGE,"E59.MirrorCS"),sQuery(id+"F22.wireOp",EDGE,"E60.MirrorCS"),sQuery(id+"F22.wireOp",EDGE,"E61.MirrorCS"),sQuery(id+"F22.wireOp",EDGE,"E62.MirrorCS"),sQuery(id+"F22.wireOp",EDGE,"E63.0"),sQuery(id+"F22.wireOp",EDGE,"E63.1"),sQuery(id+"F22.wireOp",EDGE,"E63.2"),sQuery(id+"F22.wireOp",EDGE,"E63.3"),sQuery(id+"F22.wireOp",EDGE,"E63.4"),sQuery(id+"F22.wireOp",EDGE,"E63.5"),sQuery(id+"F22.wireOp",EDGE,"E63.6"),sQuery(id+"F22.wireOp",EDGE,"E63.7"),sQuery(id+"F22.wireOp",EDGE,"E63.8"),sQuery(id+"F22.wireOp",EDGE,"E63.9"),sQuery(id+"F22.wireOp",EDGE,"E64"),sQuery(id+"F22.wireOp",EDGE,"E65")])]});
            booleanBodies(context, id + "F39", {"operationType" : BooleanOperationType.SUBTRACTION, "tools" : qUnion([Q0, Q1, Q2, Q3]), "targets" : qUnion([Q4])});
        }
        {
            var Q0;
            Q0=makeQuery(id+"F23.opExtrude","CAP_EDGE",EDGE,{"disambiguationData":[OSD([sQuery(id+"F22.wireOp",EDGE,"E64")])],"isStart":true});
            var Q1;
            Q1=makeQuery(id+"F23.opExtrude","CAP_EDGE",EDGE,{"disambiguationData":[OSD([sQuery(id+"F22.wireOp",EDGE,"E64")])],"isStart":false});
            var Q2;
            Q2=makeQuery(id+"F23.opExtrude","CAP_EDGE",EDGE,{"disambiguationData":[OSD([sQuery(id+"F22.wireOp",EDGE,"E65")])],"isStart":false});
            var Q3;
            Q3=makeQuery(id+"F23.opExtrude","CAP_EDGE",EDGE,{"disambiguationData":[OSD([sQuery(id+"F22.wireOp",EDGE,"E65")])],"isStart":true});
            fillet(context, id + "F40", {"entities" : qUnion([Q0, Q1, Q2, Q3]), "radius" : 6.35 * mm, "tangentPropagation" : true, "allowEdgeOverflow" : false});
        }
    });
